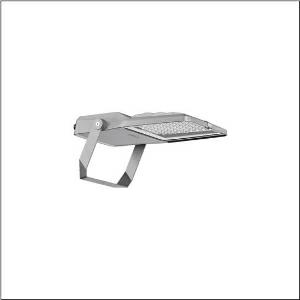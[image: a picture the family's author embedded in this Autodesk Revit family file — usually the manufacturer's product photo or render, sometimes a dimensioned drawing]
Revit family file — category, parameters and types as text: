
# Revit family: floodlight_fl_21_mini___rs12_5xa7772c4b1a_f390
name_source: partatom
category: Lighting Fixtures
units: mm (PartAtom-declared; Revit-internal decimal feet)

## family parameters
Cut with Voids When Loaded = No
Host = Face
Light Source = No
Part Type = Normal
Room Calculation Point = No
Round Connector Dimension = Use Diameter
Shared = No

## types (1)
- --- (1 x LED, 12860 lm, 87.2 W, 4000K)
    Apparent Load = 87 VA
    CIE Flux Codes = 79 92 99 100 100
    Color Rendering = 70
    Color Temperature = 4000K
    Default Elevation = 1800 mm
    Description = Floodlight FL 21 mini, floodlight, primary light control with lens, of PMMA, primary optical cover: protective disc, of toughened safety glass, transparent, light distribution: RS12, light emission: direct distribution, installation type: surface-mounted, LED, High Power LED, rated luminous flux: 12.860lm, luminous efficacy: 147lm/W, light colour: 740, colour temperature: 4000K, control gear: ECG iQ, control: Street-Remote, Auto-Match, Temp-Guard, Night-Set, Smart-Wire, Desk-Remote (wireless, voltage-free reading and setting of iQ features in the workshop via application-optimized NFC function/RFID function), optimised constant luminous flux control (CLO 2.0), with terminal, 6-pole, mains connection: 220..240V, AC, 50/60Hz, start of lifetime: 87W, end of lifetime: 92W, reduction: 40W, luminaire housing, of diecast aluminium, powder-coated, Siteco® metallic grey (DB 702S), corrosivity category C5 according to DIN EN ISO 12944, mounting bracket, of steel, galvanised, powder-coated, Siteco® metallic grey (DB 702S), protection rating (complete): IP66, insulation class (complete): insulation class II (safety insulation), certification: CE, ENEC, VDE, protection symbol: D, impact resistance: IK08, permissible operating ambient temperature: -40..+40°C, permissible operating ambient temperature for outdoor applications: -40..+50°C, standard: DIN EN 12944, packaging unit: 1 piece

Light Distribution: RS12
    Height = 70 mm
    Lamp = 1 x LED
    Lamp Light Flux = 12860 lm
    Lamp Power = 87.2 W
    Lamp count = 1
    Length = 485 mm
    Luminous efficacy = 147 lm/W
    Manufacturer = Siteco
    ModVariant = No
    Model = 5XA7772C4B1A
    Number of Poles = 1
    OnlyDefault = Yes
    Power Factor = 1
    Product Name = Floodlight FL 21 mini | RS12
    Product group = floodlight | pylon top
    ProductGroupID = 6101
    Protection Class = Protection class II
    Protection Degree = IP 66
    RLX_Detail_Level = 1
    RlxData = <blob elided: 90801 chars, md5=f4badbd3>
    Socket = socket
    Standby Power = 0 W
    System Light Flux = 12860 lm
    System Power = 87 W
    Type Comments = factory setting: luminous flux: 100 % | dim-lin: 254 | 456 mA
    Type Image = l_1006845.jpg
    URL = http://relux.com
    VarID = @adj_078631
    Voltage = 0 V
    Weight = 0.00 kg
    Width = 337 mm

## geometry (parser evidence)
native form markers: Blend x4, Sweep x13
no freeform markers — native parametric forms only
